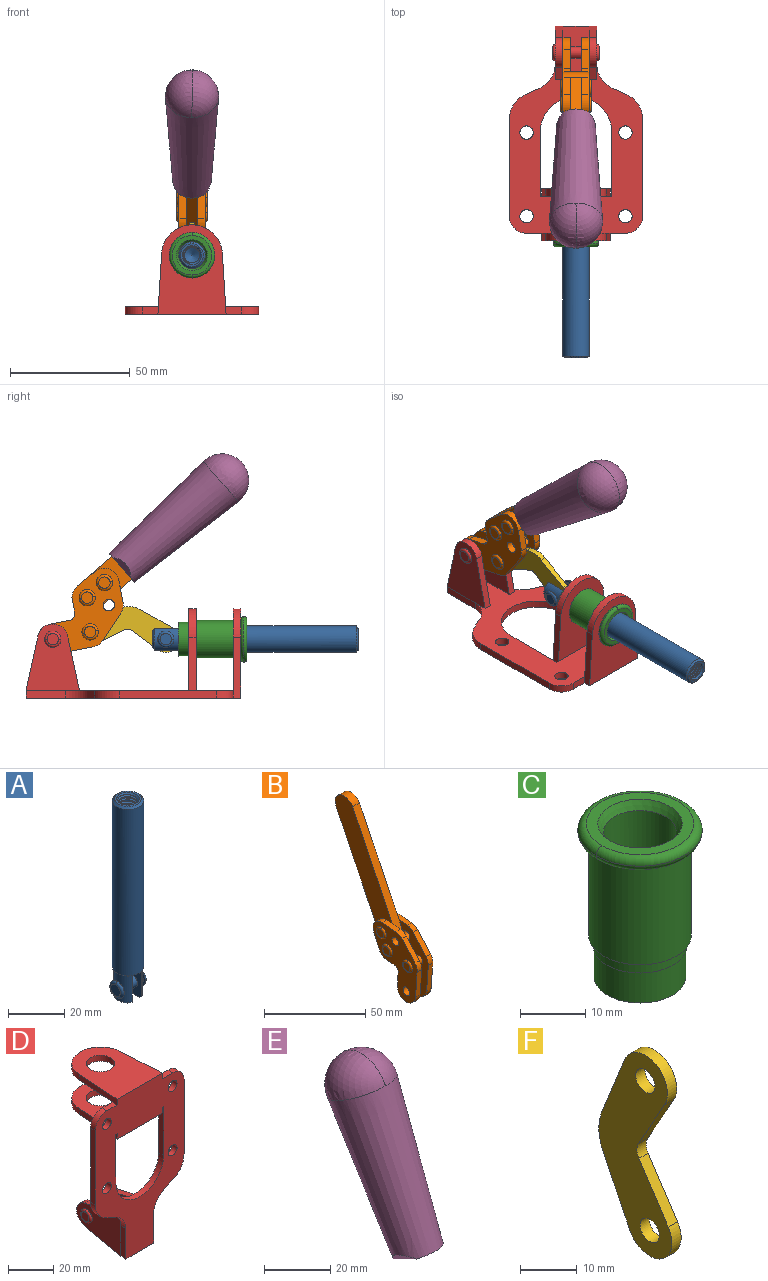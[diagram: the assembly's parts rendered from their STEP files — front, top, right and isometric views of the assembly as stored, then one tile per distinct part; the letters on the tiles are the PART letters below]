
ASSEMBLY  parts=6 mates=6
PART A: 48 faces, bbox 12.6x11.1x86.1 mm
  f0: torus R=2.41mm, axis (-1,0,0), area 15mm2, adj f30,f32,f34
  f1: torus R=2.41mm, axis (-1,0,0), area 15mm2, adj f29,f31,f33
  f2: cylinder r=5.54mm len=72.39mm, axis (0,0,1), area 2518.5mm2, adj f3,f4,f42,f43
  f3: cone r=5.54mm half-angle=45deg, axis (0,0,1), area 7.6mm2, adj f2,f5,f41
  f4: cone r=5.54mm half-angle=45deg, axis (0,0,-1), area 34.9mm2, adj f2,f39
  f5: cylinder r=5.08mm len=11.48mm, axis (0,0,1), area 108.3mm2, adj f3,f7,f8,f41
  f6: cylinder r=2.41mm len=4.83mm, axis (-1,0,0), area 71.2mm2, adj f40,f41
  f7: cylinder r=2.41mm len=4.83mm, axis (-1,0,0), area 7.6mm2, adj f5,f34
  f8: cone r=5.08mm half-angle=45deg, axis (0,0,1), area 10.6mm2, adj f5,f37,f41
  f9: cone r=3.98mm half-angle=45deg, axis (0,0,1), area 17.6mm2, adj f27,f39,f45,f46,f47
  f10: cylinder r=2.41mm len=4.83mm, axis (-1,0,0), area 7.6mm2, adj f33,f38
  f11: cylinder r=3.2mm len=6.4mm, axis (0,0,1), area 78.4mm2, adj f12,f28,f44,f45,f47
  f12: cylinder r=3.2mm len=6.4mm, axis (0,0,1), area 10.5mm2, adj f11,f13,f45,f47
  f13: cylinder r=3.2mm len=6.4mm, axis (0,0,1), area 10.5mm2, adj f12,f14,f45,f47
  f14: cylinder r=3.2mm len=6.4mm, axis (0,0,1), area 10.5mm2, adj f13,f15,f45,f47
  f15: cylinder r=3.2mm len=6.4mm, axis (0,0,1), area 10.5mm2, adj f14,f16,f45,f47
  f16: cylinder r=3.2mm len=6.4mm, axis (0,0,1), area 10.5mm2, adj f15,f17,f45,f47
  f17: cylinder r=3.2mm len=6.4mm, axis (0,0,1), area 10.5mm2, adj f16,f18,f45,f47
  f18: cylinder r=3.2mm len=6.4mm, axis (0,0,1), area 10.5mm2, adj f17,f19,f45,f47
  f19: cylinder r=3.2mm len=6.4mm, axis (0,0,1), area 10.5mm2, adj f18,f20,f45,f47
  f20: cylinder r=3.2mm len=6.4mm, axis (0,0,1), area 10.5mm2, adj f19,f21,f45,f47
  f21: cylinder r=3.2mm len=6.4mm, axis (0,0,1), area 10.5mm2, adj f20,f22,f45,f47
  f22: cylinder r=3.2mm len=6.4mm, axis (0,0,1), area 10.5mm2, adj f21,f23,f45,f47
  f23: cylinder r=3.2mm len=6.4mm, axis (0,0,1), area 10.5mm2, adj f22,f24,f45,f47
  f24: cylinder r=3.2mm len=6.4mm, axis (0,0,1), area 10.5mm2, adj f23,f25,f45,f47
  f25: cylinder r=3.2mm len=6.4mm, axis (0,0,1), area 10.5mm2, adj f24,f26,f45,f47
  f26: cylinder r=3.2mm len=6.4mm, axis (0,0,1), area 10.5mm2, adj f25,f27,f45,f47
  f27: cylinder r=3.2mm len=6.4mm, axis (0,0,1), area 7.4mm2, adj f9,f26,f45,f47
  f28: cone r=3.2mm half-angle=60deg, axis (0,0,1), area 37.2mm2, adj f11
  f29: plane 4.83x4.83mm, normal (-1,0,0), area 18.3mm2, adj f1,f31
  f30: plane 4.83x4.83mm, normal (1,0,0), area 18.3mm2, adj f0,f32
  f31: torus R=2.41mm, axis (-1,0,0), area 15mm2, adj f1,f29,f33
  f32: torus R=2.41mm, axis (-1,0,0), area 15mm2, adj f0,f30,f34
  f33: plane 6.83x6.83mm, normal (1,0,0), area 18.3mm2, adj f1,f10,f31
  f34: plane 6.83x6.83mm, normal (-1,0,0), area 18.3mm2, adj f0,f7,f32
  f35: cone r=5.08mm half-angle=45deg, axis (0,0,1), area 10.6mm2, adj f36,f38,f40
  f36: plane 7.25x1.97mm, normal (0,0,-1), area 10mm2, adj f35,f40
  f37: plane 7.25x1.97mm, normal (0,0,-1), area 10mm2, adj f8,f41
  f38: cylinder r=5.08mm len=11.48mm, axis (0,0,1), area 108.3mm2, adj f10,f35,f40,f42
  f39: plane 9.55x9.55mm, normal (0,0,1), area 22mm2, adj f4,f9
  f40: plane 12.76x10.09mm, normal (1,0,0), area 95.7mm2, adj f6,f35,f36,f38,f42,f43
  f41: plane 12.76x10.09mm, normal (-1,0,0), area 95.7mm2, adj f3,f5,f6,f8,f37,f43
  f42: cone r=5.54mm half-angle=45deg, axis (0,0,1), area 7.6mm2, adj f2,f38,f40
  f43: plane 11.07x4.7mm, normal (0,0,-1), area 50.4mm2, adj f2,f40,f41
  f44: plane 0.89x0.62mm, normal (-1,0,0), area 0.3mm2, adj f11,f45,f46,f47
  f45: bspline ~24.8x7.63mm, area 266.6mm2, adj f9,f11,f12,f13,f14,f15,f16,f17
  f46: bspline ~24.87x7.63mm, area 73.6mm2, adj f9,f44,f45,f47
  f47: bspline ~24.98x7.63mm, area 272.5mm2, adj f9,f11,f12,f13,f14,f15,f16,f17
PART B: 59 faces, bbox 12.9x60.2x99.6 mm
  f0: torus R=2.39mm, axis (-1,0,0), area 14.9mm2, adj f20,f43,f51
  f1: torus R=2.39mm, axis (-1,0,0), area 14.9mm2, adj f19,f42,f51
  f2: torus R=2.39mm, axis (-1,0,0), area 14.9mm2, adj f18,f35,f51
  f3: torus R=2.39mm, axis (-1,0,0), area 14.9mm2, adj f14,f17,f23
  f4: torus R=2.39mm, axis (-1,0,0), area 14.9mm2, adj f13,f16,f23
  f5: torus R=2.39mm, axis (-1,0,0), area 14.9mm2, adj f12,f15,f23
  f6: cylinder r=2.39mm len=4.78mm, axis (1,0,0), area 46.5mm2, adj f48,f50,f51
  f7: cylinder r=2.39mm len=4.78mm, axis (1,0,0), area 46.5mm2, adj f50,f51
  f8: cylinder r=6.35mm len=12.68mm, axis (1,0,0), area 61.8mm2, adj f38,f39,f50,f51
  f9: cylinder r=2.39mm len=4.78mm, axis (-1,0,0), area 70.5mm2, adj f46,f50
  f10: cylinder r=2.39mm len=4.78mm, axis (-1,0,0), area 46.5mm2, adj f23,f45,f46
  f11: cylinder r=2.39mm len=4.78mm, axis (-1,0,0), area 46.5mm2, adj f23,f46
  f12: plane 4.78x4.78mm, normal (1,0,0), area 17.9mm2, adj f5,f15
  f13: plane 4.78x4.78mm, normal (1,0,0), area 17.9mm2, adj f4,f16
  f14: plane 4.78x4.78mm, normal (1,0,0), area 17.9mm2, adj f3,f17
  f15: torus R=2.39mm, axis (-1,0,0), area 14.9mm2, adj f5,f12,f23
  f16: torus R=2.39mm, axis (-1,0,0), area 14.9mm2, adj f4,f13,f23
  f17: torus R=2.39mm, axis (-1,0,0), area 14.9mm2, adj f3,f14,f23
  f18: plane 4.78x4.78mm, normal (-1,0,0), area 17.9mm2, adj f2,f35
  f19: plane 4.78x4.78mm, normal (-1,0,0), area 17.9mm2, adj f1,f42
  f20: plane 4.78x4.78mm, normal (-1,0,0), area 17.9mm2, adj f0,f43
  f21: plane 2.26x0.2mm, normal (1,0,0), area 0.2mm2, adj f31,f44
  f22: plane 2.26x0.2mm, normal (-1,0,0), area 0.2mm2, adj f41,f44
  f23: plane 39.37x30.77mm, normal (1,0,0), area 565.5mm2, adj f3,f4,f5,f10,f11,f15,f16,f17
  f24: cylinder r=6.1mm len=4.15mm, axis (-1,0,0), area 14.7mm2, adj f23,f25,f32,f46
  f25: plane 10.25x9.01mm, normal (0,-0.75,0.66), area 42.3mm2, adj f23,f24,f26,f46
  f26: cylinder r=6.35mm len=4.64mm, axis (-1,0,0), area 15.6mm2, adj f23,f25,f27,f46
  f27: plane 15.84x3.1mm, normal (0,-1,-0.07), area 49.2mm2, adj f23,f26,f28,f46
  f28: cylinder r=6.35mm len=12.68mm, axis (-1,0,0), area 61.8mm2, adj f23,f27,f29,f46
  f29: plane 8.11x3.1mm, normal (0,1,0.07), area 25.2mm2, adj f23,f28,f30,f46
  f30: cylinder r=3.05mm len=3.25mm, axis (-1,0,0), area 14.8mm2, adj f23,f29,f31,f46
  f31: plane 5.99x3.1mm, normal (0,0.07,-1), area 18.6mm2, adj f21,f23,f30,f44,f46
  f32: plane 9.5x3.1mm, normal (0,-0.07,1), area 29.5mm2, adj f23,f24,f33,f46,f47
  f33: cylinder r=6.1mm len=8.63mm, axis (-1,0,0), area 39.1mm2, adj f23,f32,f34,f47
  f34: plane 8.65x3.96mm, normal (0,0.91,-0.42), area 29.5mm2, adj f23,f33,f44,f47
  f35: torus R=2.39mm, axis (-1,0,0), area 14.9mm2, adj f2,f18,f51
  f36: plane 10.25x9.01mm, normal (0,-0.75,0.66), area 42.3mm2, adj f37,f49,f50,f51
  f37: cylinder r=6.35mm len=4.64mm, axis (1,0,0), area 15.6mm2, adj f36,f38,f50,f51
  f38: plane 15.84x3.1mm, normal (0,-1,-0.07), area 49.2mm2, adj f8,f37,f50,f51
  f39: plane 8.11x3.1mm, normal (0,1,0.07), area 25.2mm2, adj f8,f40,f50,f51
  f40: cylinder r=3.05mm len=3.25mm, axis (1,0,0), area 14.8mm2, adj f39,f41,f50,f51
  f41: plane 5.99x3.1mm, normal (0,0.07,-1), area 18.6mm2, adj f22,f40,f44,f50,f51
  f42: torus R=2.39mm, axis (-1,0,0), area 14.9mm2, adj f1,f19,f51
  f43: torus R=2.39mm, axis (-1,0,0), area 14.9mm2, adj f0,f20,f51
  f44: cylinder r=6.35mm len=12.12mm, axis (-1,0,0), area 128.9mm2, adj f21,f22,f23,f31,f34,f41,f46,f47
  f45: plane 2.65x1.35mm, normal (1,0,0), area 1mm2, adj f10,f55
  f46: plane 39.08x20.42mm, normal (-1,0,0), area 412.5mm2, adj f9,f10,f11,f24,f25,f26,f27,f28
  f47: plane 77.62x39.82mm, normal (1,0,0), area 850mm2, adj f32,f33,f34,f44,f53,f54,f55
  f48: plane 2.65x1.35mm, normal (-1,0,0), area 1mm2, adj f6,f55
  f49: cylinder r=6.1mm len=4.15mm, axis (1,0,0), area 14.7mm2, adj f36,f50,f51,f56
  f50: plane 39.08x20.42mm, normal (1,0,0), area 412.5mm2, adj f6,f7,f8,f9,f36,f37,f38,f39
  f51: plane 39.37x30.77mm, normal (-1,0,0), area 565.5mm2, adj f0,f1,f2,f6,f7,f8,f35,f36
  f52: plane 8.65x3.96mm, normal (0,0.91,-0.42), area 29.5mm2, adj f44,f51,f57,f58
  f53: plane 68.49x33.4mm, normal (0,0.9,-0.44), area 358.1mm2, adj f44,f47,f54,f58
  f54: cylinder r=6.35mm len=12.06mm, axis (1,0,0), area 93.7mm2, adj f47,f53,f55,f58
  f55: plane 68.49x33.4mm, normal (0,-0.9,0.44), area 358.1mm2, adj f44,f45,f46,f47,f48,f50,f54,f58
  f56: plane 9.5x3.1mm, normal (0,-0.07,1), area 29.5mm2, adj f49,f50,f51,f57,f58
  f57: cylinder r=6.1mm len=8.63mm, axis (1,0,0), area 39.1mm2, adj f51,f52,f56,f58
  f58: plane 77.62x39.82mm, normal (-1,0,0), area 850mm2, adj f44,f52,f53,f54,f55,f56,f57
PART C: 15 faces, bbox 20.6x20.6x28.7 mm
  f0: torus R=8.26mm, axis (0,0,1), area 56.8mm2, adj f1,f10,f12
  f1: torus R=8.26mm, axis (0,0,1), area 56.8mm2, adj f0,f6,f13
  f2: cylinder r=5.59mm len=25.91mm, axis (0,0,1), area 909.6mm2, adj f3,f4
  f3: cone r=6.86mm half-angle=45deg, axis (0,0,-1), area 70.2mm2, adj f2,f14
  f4: cone r=6.47mm half-angle=30deg, axis (0,0,1), area 66.7mm2, adj f2,f13
  f5: cylinder r=7.04mm len=14.07mm, axis (0,0,1), area 252.6mm2, adj f11,f14
  f6: torus R=8.26mm, axis (0,0,1), area 56.8mm2, adj f1,f12,f13
  f7: cylinder r=7.16mm len=14.33mm, axis (0,0,1), area 91.5mm2, adj f9,f11
  f8: cylinder r=7.86mm len=18.42mm, axis (0,0,1), area 909.6mm2, adj f9,f10
  f9: plane 15.72x15.72mm, normal (0,0,-1), area 33mm2, adj f7,f8
  f10: plane 16.51x16.51mm, normal (0,0,-1), area 19.9mm2, adj f0,f8,f12
  f11: plane 14.33x14.33mm, normal (0,0,-1), area 5.7mm2, adj f5,f7
  f12: torus R=8.26mm, axis (0,0,1), area 56.8mm2, adj f0,f6,f10
  f13: plane 16.51x16.51mm, normal (0,0,1), area 82.7mm2, adj f1,f4,f6
  f14: plane 14.07x14.07mm, normal (0,0,-1), area 7.8mm2, adj f3,f5
PART D: 55 faces, bbox 55.7x37.4x89.8 mm
  f0: torus R=2.41mm, axis (-1,0,0), area 15mm2, adj f11,f15,f25
  f1: torus R=2.41mm, axis (-1,0,0), area 15mm2, adj f10,f12,f22
  f2: cylinder r=2.78mm len=5.56mm, axis (0,-1,0), area 54.2mm2, adj f30,f54
  f3: cylinder r=14.99mm len=29.97mm, axis (0,-1,0), area 145.9mm2, adj f30,f49,f53,f54
  f4: cylinder r=2.78mm len=5.56mm, axis (0,-1,0), area 54.2mm2, adj f30,f54
  f5: cylinder r=2.78mm len=5.56mm, axis (0,-1,0), area 54.2mm2, adj f30,f54
  f6: cylinder r=2.78mm len=5.56mm, axis (0,-1,0), area 54.2mm2, adj f30,f54
  f7: cylinder r=6.35mm len=12.7mm, axis (0,0,1), area 123.6mm2, adj f27,f51
  f8: cylinder r=6.35mm len=12.7mm, axis (0,0,-1), area 124.7mm2, adj f21,f35
  f9: cylinder r=2.41mm len=11.18mm, axis (-1,0,0), area 169.4mm2, adj f16,f19
  f10: plane 4.83x4.83mm, normal (1,0,0), area 18.3mm2, adj f1,f12
  f11: plane 4.83x4.83mm, normal (-1,0,0), area 18.3mm2, adj f0,f15
  f12: torus R=2.41mm, axis (-1,0,0), area 15mm2, adj f1,f10,f22
  f13: cylinder r=6.35mm len=12.41mm, axis (1,0,0), area 53.4mm2, adj f18,f19,f22,f23
  f14: cylinder r=6.35mm len=12.41mm, axis (-1,0,0), area 53.4mm2, adj f16,f17,f24,f25
  f15: torus R=2.41mm, axis (-1,0,0), area 15mm2, adj f0,f11,f25
  f16: plane 27.86x22.35mm, normal (1,0,0), area 425.4mm2, adj f9,f14,f17,f24,f30
  f17: plane 22.86x4.97mm, normal (0,0.21,0.98), area 72.5mm2, adj f14,f16,f25,f30
  f18: plane 22.86x4.97mm, normal (0,0.21,0.98), area 72.5mm2, adj f13,f19,f22,f30
  f19: plane 27.86x22.35mm, normal (-1,0,0), area 425.4mm2, adj f9,f13,f18,f23,f30
  f20: cylinder r=12.7mm len=25.35mm, axis (0,0,-1), area 119.8mm2, adj f21,f34,f35,f36
  f21: plane 34.21x28.07mm, normal (0,0,-1), area 702.4mm2, adj f8,f20,f30,f34,f36
  f22: plane 27.96x22.45mm, normal (1,0,0), area 407.2mm2, adj f1,f12,f13,f18,f23,f30,f42,f43
  f23: plane 22.86x4.97mm, normal (0,0.21,-0.98), area 72.5mm2, adj f13,f19,f22,f44
  f24: plane 22.86x4.97mm, normal (0,0.21,-0.98), area 72.5mm2, adj f14,f16,f25,f44
  f25: plane 27.86x22.35mm, normal (-1,0,0), area 407.1mm2, adj f0,f14,f15,f17,f24,f30,f45,f46
  f26: plane 3.1x0.95mm, normal (0,0,-1), area 2.7mm2, adj f30,f49,f50,f54
  f27: plane 34.21x28.07mm, normal (0,0,1), area 702.4mm2, adj f7,f28,f30,f50,f52
  f28: cylinder r=12.7mm len=25.35mm, axis (0,0,1), area 118.8mm2, adj f27,f50,f51,f52
  f29: plane 3.1x0.95mm, normal (0,0,-1), area 2.7mm2, adj f30,f52,f53,f54
  f30: plane 86.54x55.63mm, normal (0,1,0), area 2362.9mm2, adj f2,f3,f4,f5,f6,f16,f17,f18
  f31: plane 40.56x3.1mm, normal (-1,0,0), area 125.7mm2, adj f30,f32,f48,f54
  f32: cylinder r=7.11mm len=7.11mm, axis (0,-1,0), area 34.6mm2, adj f30,f31,f33,f54
  f33: plane 6.67x3.1mm, normal (0,0,1), area 20.4mm2, adj f30,f32,f34,f54
  f34: plane 25.39x3.13mm, normal (-1,0.06,0), area 79.5mm2, adj f20,f21,f33,f35,f54
  f35: plane 37.31x28.45mm, normal (0,0,1), area 789.9mm2, adj f8,f20,f34,f36,f54
  f36: plane 25.39x3.13mm, normal (1,0.06,0), area 79.5mm2, adj f20,f21,f35,f37,f54
  f37: plane 6.67x3.1mm, normal (0,0,1), area 20.4mm2, adj f30,f36,f38,f54
  f38: cylinder r=7.11mm len=7.11mm, axis (0,-1,0), area 34.6mm2, adj f30,f37,f39,f54
  f39: plane 40.56x3.1mm, normal (1,0,0), area 125.7mm2, adj f30,f38,f40,f54
  f40: cylinder r=11.18mm len=10.16mm, axis (0,-1,0), area 39.5mm2, adj f30,f39,f41,f54
  f41: plane 6.09x3.1mm, normal (0.42,0,-0.91), area 20.8mm2, adj f30,f40,f42,f54
  f42: cylinder r=11.18mm len=9.41mm, axis (0,-1,0), area 37.2mm2, adj f22,f30,f41,f43,f54
  f43: plane 16.5x3.1mm, normal (1,0,0), area 51.1mm2, adj f22,f42,f44,f54
  f44: plane 17.37x3.1mm, normal (0,0,-1), area 53.8mm2, adj f23,f24,f30,f43,f45,f54
  f45: plane 16.5x3.1mm, normal (-1,0,0), area 51.1mm2, adj f25,f44,f46,f54
  f46: cylinder r=11.18mm len=9.41mm, axis (0,-1,0), area 37.2mm2, adj f25,f30,f45,f47,f54
  f47: plane 6.09x3.1mm, normal (-0.42,0,-0.91), area 20.8mm2, adj f30,f46,f48,f54
  f48: cylinder r=11.18mm len=10.16mm, axis (0,-1,0), area 39.5mm2, adj f30,f31,f47,f54
  f49: plane 26.54x3.1mm, normal (-1,0,0), area 82.3mm2, adj f3,f26,f30,f54
  f50: plane 25.39x3.1mm, normal (1,0.06,0), area 78.8mm2, adj f26,f27,f28,f51,f54
  f51: plane 37.31x28.45mm, normal (0,0,-1), area 789.9mm2, adj f7,f28,f50,f52,f54
  f52: plane 25.39x3.1mm, normal (-1,0.06,0), area 78.8mm2, adj f27,f28,f29,f51,f54
  f53: plane 26.54x3.1mm, normal (1,0,0), area 82.3mm2, adj f3,f29,f30,f54
  f54: plane 89.66x55.63mm, normal (0,-1,0), area 2678.5mm2, adj f2,f3,f4,f5,f6,f26,f29,f31
PART E: 11 faces, bbox 22.3x42.6x64.5 mm
  f0: sphere r=11.13mm, area 411.4mm2, adj f1,f8
  f1: cone r=11.11mm half-angle=3.3deg, axis (0,0.44,0.9), area 3251.8mm2, adj f0,f7,f8,f9,f10
  f2: cylinder r=6.16mm len=11.7mm, axis (1,0,0), area 89.5mm2, adj f3,f4,f5,f6
  f3: plane 60.23x36.75mm, normal (-1,0,0), area 763.6mm2, adj f2,f4,f6,f10
  f4: plane 51.37x25.05mm, normal (0,0.9,-0.44), area 264.2mm2, adj f2,f3,f5,f10
  f5: plane 60.23x36.75mm, normal (1,0,0), area 763.6mm2, adj f2,f4,f6,f10
  f6: plane 51.37x25.05mm, normal (0,-0.9,0.44), area 264.2mm2, adj f2,f3,f5,f10
  f7: plane 9.95x5.95mm, normal (0.71,-0.31,-0.64), area 25.8mm2, adj f1,f10
  f8: sphere r=11.13mm, area 411.4mm2, adj f0,f1
  f9: plane 9.95x5.95mm, normal (-0.71,-0.31,-0.64), area 25.8mm2, adj f1,f10
  f10: plane 14.27x11.38mm, normal (0,-0.44,-0.9), area 106.7mm2, adj f1,f3,f4,f5,f6,f7,f9
PART F: 12 faces, bbox 2.3x18.2x42.8 mm
  f0: cylinder r=2.4mm len=4.8mm, axis (1,0,0), area 34.9mm2, adj f4,f11
  f1: cylinder r=10.41mm len=8.47mm, axis (1,0,0), area 20.2mm2, adj f4,f9,f10,f11
  f2: cylinder r=3.05mm len=3.16mm, axis (1,0,0), area 7.7mm2, adj f4,f6,f7,f11
  f3: cylinder r=2.4mm len=4.8mm, axis (1,0,0), area 34.9mm2, adj f4,f11
  f4: plane 42.81x18.23mm, normal (-1,0,0), area 414.1mm2, adj f0,f1,f2,f3,f5,f6,f7,f8
  f5: cylinder r=5.54mm len=10.67mm, axis (1,0,0), area 41.8mm2, adj f4,f6,f10,f11
  f6: plane 11.66x6.53mm, normal (0,-0.87,-0.49), area 30.9mm2, adj f2,f4,f5,f11
  f7: plane 11.17x7.33mm, normal (0,-0.84,0.55), area 30.9mm2, adj f2,f4,f8,f11
  f8: cylinder r=5.54mm len=10.51mm, axis (1,0,0), area 41.8mm2, adj f4,f7,f9,f11
  f9: plane 13.67x6.67mm, normal (0,0.9,-0.44), area 35.1mm2, adj f1,f4,f8,f11
  f10: plane 14.1x5.7mm, normal (0,0.93,0.37), area 35.1mm2, adj f1,f4,f5,f11
  f11: plane 42.81x18.23mm, normal (1,0,0), area 414.1mm2, adj f0,f1,f2,f3,f5,f6,f7,f8
PLACE A rot(axis=(1,0,0),90deg) t=(0,9.81,0)mm
PLACE B rot(axis=(1,0,0),75deg) t=(0,4.15,9.14)mm
PLACE C rot(axis=(0.58,-0.58,0.58),120deg) t=(24.61,9.43,24.61)mm
PLACE D rot(axis=(1,0,0),90deg) t=(0,9.43,0)mm fixed
PLACE E rot(axis=(1,0,0),75deg) t=(0,4.15,9.14)mm
PLACE F rot(axis=(0,0.69,0.73),180deg) t=(0,11.99,2.14)mm
MATE fastened E.f2 <-> B.f54  axis (1,0,0) through (0,-30.37,91.94)mm
MATE fastened C.f2 <-> D.f7  axis (0,1,0) through (0,-36.96,24.61)mm
MATE revolute F.f5 <-> B.f4  axis (-1,0,0) through (0,25.94,27.64)mm
MATE revolute D.f0 <-> B.f7  axis (-1,0,0) through (0,41.52,24.61)mm
MATE slider A.f2 <-> D.f7  axis (0,-1,0) through (0,-48.97,24.61)mm
MATE revolute F.f3 <-> A.f6  axis (-1,0,0) through (0,-5.67,24.61)mm
